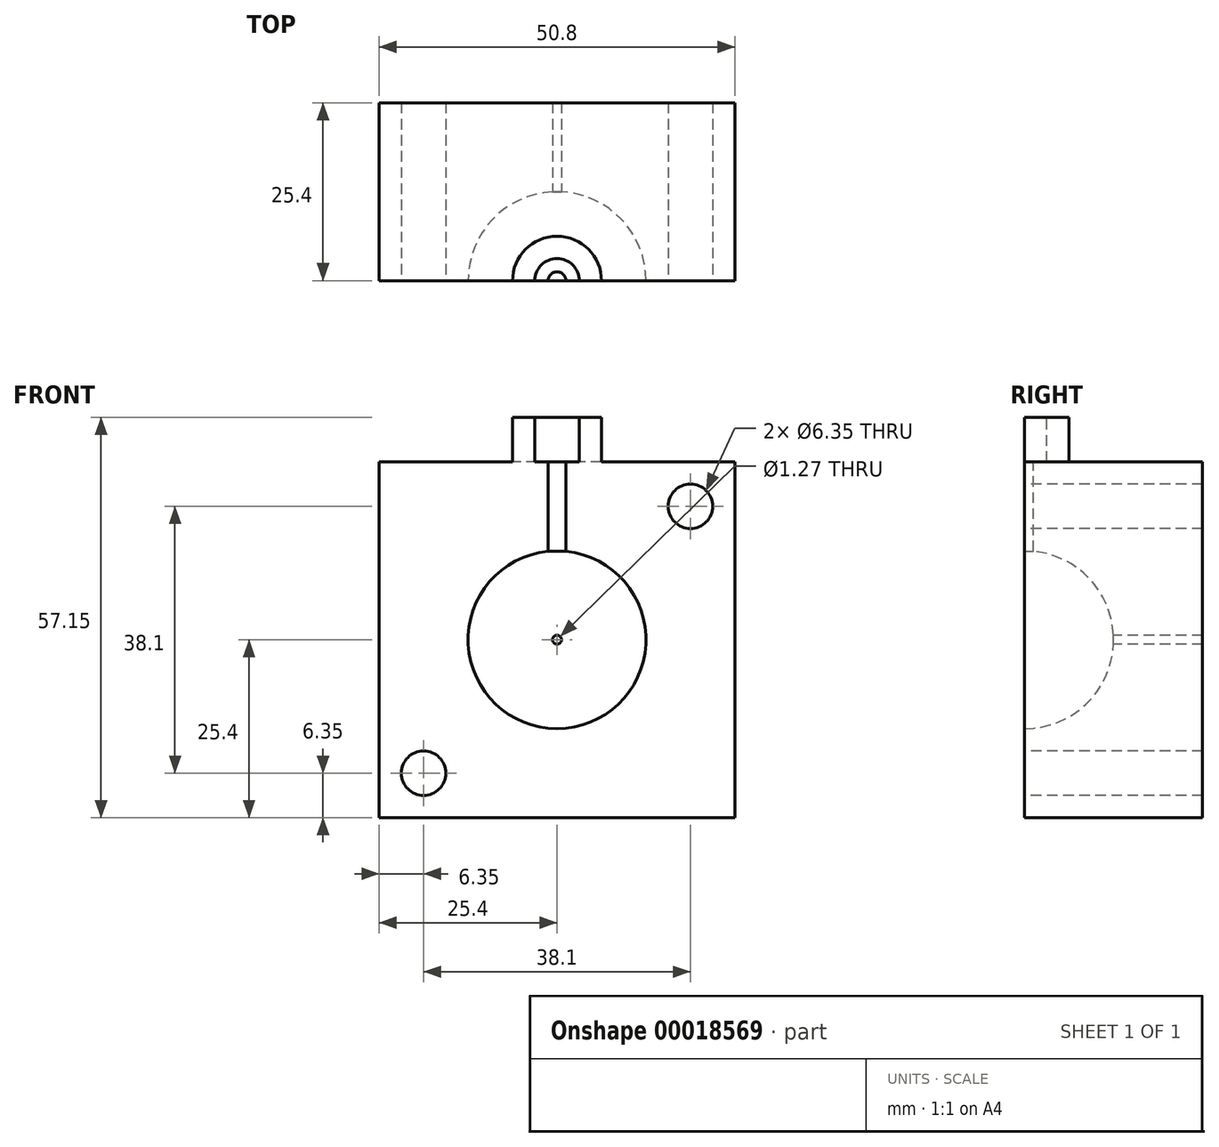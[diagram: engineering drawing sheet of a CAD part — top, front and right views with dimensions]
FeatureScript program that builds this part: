
annotation { "Feature Type Name" : "Feature", "Feature Type Description" : "" }
export const myFeature = defineFeature(function(context is Context, id is Id, definition is map)
    precondition{}
    {
        {
            var Q0;
            Q0=qCreatedBy(makeId("Front.planeOp"),FACE);
            var sketch = newSketch(context, id + "F0", { "sketchPlane" : qUnion([Q0])});
            skLineSegment(sketch, "E0.bottom", {"start": v(0, 0) * mm, "end": v(50.8, 0) * mm});
            skLineSegment(sketch, "E0.top", {"start": v(0, 50.8) * mm, "end": v(50.8, 50.8) * mm});
            skLineSegment(sketch, "E0.left", {"start": v(0, 0) * mm, "end": v(0, 50.8) * mm});
            skLineSegment(sketch, "E0.right", {"start": v(50.8, 0) * mm, "end": v(50.8, 50.8) * mm});
            skSolve(sketch);
        }
        {
            var Q0;
            Q0 = qSketchRegion(id + "F0", true);
            extrude(context, id + "F9", {"entities" : qUnion([Q0]), "depth" : 25.4 * mm});
        }
        {
            var Q0;
            Q0=makeQuery(id+"F9.opExtrude","CAP_FACE",FACE,{"disambiguationData":[OSD([sQuery(id+"F0.wireOp",EDGE,"E0.bottom"),sQuery(id+"F0.wireOp",EDGE,"E0.top"),sQuery(id+"F0.wireOp",EDGE,"E0.left"),sQuery(id+"F0.wireOp",EDGE,"E0.right")])],"isStart":false});
            var sketch = newSketch(context, id + "F1", { "sketchPlane" : qUnion([Q0])});
            skLineSegment(sketch, "E1", {"start": v(25.4, 50.8) * mm, "end": v(25.4, 0) * mm});
            skArc(sketch, "E2", {"start": v(25.4, 12.7) * mm, "mid": v(38.1, 25.4) * mm, "end": v(25.4, 38.1) * mm});
            skSolve(sketch);
        }
        {
            var Q0;
            Q0 = qSketchRegion(id + "F1", true);
            var Q1;
            Q1=sQuery(id+"F1.wireOp",EDGE,"E1");
            revolve(context, id + "F10", {"operationType" : NewBodyOperationType.REMOVE, "entities" : qUnion([Q0]), "axis" : qUnion([Q1]), "revolveType" : RevolveType.FULL, "oppositeDirection" : true});
        }
        {
            var Q0;
            Q0=makeQuery(id+"F9.opExtrude","CAP_FACE",FACE,{"disambiguationData":[OSD([sQuery(id+"F0.wireOp",EDGE,"E0.bottom"),sQuery(id+"F0.wireOp",EDGE,"E0.top"),sQuery(id+"F0.wireOp",EDGE,"E0.left"),sQuery(id+"F0.wireOp",EDGE,"E0.right")])],"isStart":false});
            var sketch = newSketch(context, id + "F11", { "sketchPlane" : qUnion([Q0])});
            skLineSegment(sketch, "E3", {"start": v(0, 0) * mm, "end": v(0, 6.35) * mm});
            skLineSegment(sketch, "E4", {"start": v(0, 0) * mm, "end": v(6.35, 0) * mm});
            skCircle(sketch, "E5", {"center": v(6.35, 6.35) * mm, "radius": 3.18 * mm});
            skSolve(sketch);
        }
        {
            var Q0;
            Q0 = qSketchRegion(id + "F11", true);
            extrude(context, id + "F2", {"entities" : qUnion([Q0]), "operationType" : NewBodyOperationType.REMOVE, "endBound" : BoundingType.THROUGH_ALL, "oppositeDirection" : true, "depth" : 25.4 * mm});
        }
        {
            var Q0;
            Q0=makeQuery(id+"F9.opExtrude","CAP_FACE",FACE,{"disambiguationData":[OSD([sQuery(id+"F0.wireOp",EDGE,"E0.bottom"),sQuery(id+"F0.wireOp",EDGE,"E0.top"),sQuery(id+"F0.wireOp",EDGE,"E0.left"),sQuery(id+"F0.wireOp",EDGE,"E0.right")])],"isStart":false});
            var sketch = newSketch(context, id + "F3", { "sketchPlane" : qUnion([Q0])});
            skLineSegment(sketch, "E6", {"start": v(50.8, 50.8) * mm, "end": v(44.45, 50.8) * mm});
            skLineSegment(sketch, "E7", {"start": v(50.8, 50.8) * mm, "end": v(50.8, 44.45) * mm});
            skCircle(sketch, "E8", {"center": v(44.45, 44.45) * mm, "radius": 3.18 * mm});
            skSolve(sketch);
        }
        {
            var Q0;
            Q0 = qSketchRegion(id + "F3", true);
            extrude(context, id + "F4", {"entities" : qUnion([Q0]), "operationType" : NewBodyOperationType.REMOVE, "endBound" : BoundingType.THROUGH_ALL, "oppositeDirection" : true, "depth" : 25.4 * mm});
        }
        {
            var Q0;
            Q0=makeQuery(id+"F9.opExtrude","SWEPT_FACE",FACE,{"disambiguationData":[OSD([sQuery(id+"F0.wireOp",EDGE,"E0.top")])]});
            var sketch = newSketch(context, id + "F5", { "sketchPlane" : qUnion([Q0])});
            skPoint(sketch, "E9.start.orphan", {"position": v(25.4, -25.4) * mm});
            skLineSegment(sketch, "E10", {"start": v(19.05, -25.4) * mm, "end": v(31.75, -25.4) * mm});
            skArc(sketch, "E11", {"start": v(31.75, -25.4) * mm, "mid": v(25.4, -19.05) * mm, "end": v(19.05, -25.4) * mm});
            skSolve(sketch);
        }
        {
            var Q0;
            Q0 = qSketchRegion(id + "F5", true);
            extrude(context, id + "F6", {"entities" : qUnion([Q0]), "operationType" : NewBodyOperationType.ADD, "depth" : 6.35 * mm});
        }
        {
            var Q0;
            Q0=makeQuery(id+"F6.opExtrude","CAP_FACE",FACE,{"disambiguationData":[OSD([sQuery(id+"F5.wireOp",EDGE,"E10"),sQuery(id+"F5.wireOp",EDGE,"E11")])],"isStart":false});
            var sketch = newSketch(context, id + "F7", { "sketchPlane" : qUnion([Q0])});
            skLineSegment(sketch, "E12", {"start": v(22.23, -25.4) * mm, "end": v(28.58, -25.4) * mm});
            skArc(sketch, "E13", {"start": v(28.58, -25.4) * mm, "mid": v(25.4, -22.23) * mm, "end": v(22.23, -25.4) * mm});
            skPoint(sketch, "E14.orphan", {"position": v(19.05, -25.4) * mm});
            skPoint(sketch, "E15.orphan", {"position": v(31.75, -25.4) * mm});
            skSolve(sketch);
        }
        {
            var Q0;
            Q0 = qSketchRegion(id + "F7", true);
            extrude(context, id + "F12", {"entities" : qUnion([Q0]), "operationType" : NewBodyOperationType.REMOVE, "oppositeDirection" : true, "depth" : 6.35 * mm});
        }
        {
            var Q0;
            Q0=makeQuery(id+"F12.boolean.opBoolean","COPY",FACE,{"derivedFrom":makeQuery(id+"F12.opExtrude","CAP_FACE",FACE,{"disambiguationData":[OSD([sQuery(id+"F7.wireOp",EDGE,"E12"),sQuery(id+"F7.wireOp",EDGE,"E13")])],"isStart":false})});
            var sketch = newSketch(context, id + "F13", { "sketchPlane" : qUnion([Q0])});
            skLineSegment(sketch, "E16", {"start": v(22.23, -25.4) * mm, "end": v(28.58, -25.4) * mm});
            skCircle(sketch, "E17", {"center": v(25.4, -25.4) * mm, "radius": 1.27 * mm});
            skSolve(sketch);
        }
        {
            var Q0;
            Q0 = qSketchRegion(id + "F13", true);
            extrude(context, id + "F8", {"entities" : qUnion([Q0]), "operationType" : NewBodyOperationType.REMOVE, "oppositeDirection" : true, "depth" : 25.4 * mm});
        }
        {
            var Q0;
            Q0=makeQuery(id+"F6.boolean.opBoolean","MERGE",FACE,{"derivedFrom":[makeQuery(id+"F9.opExtrude","CAP_FACE",FACE,{"disambiguationData":[OSD([sQuery(id+"F0.wireOp",EDGE,"E0.bottom"),sQuery(id+"F0.wireOp",EDGE,"E0.top"),sQuery(id+"F0.wireOp",EDGE,"E0.left"),sQuery(id+"F0.wireOp",EDGE,"E0.right")])],"isStart":false}),makeQuery(id+"F6.opExtrude","SWEPT_FACE",FACE,{"disambiguationData":[OSD([sQuery(id+"F5.wireOp",EDGE,"E10")])]})]});
            var sketch = newSketch(context, id + "F14", { "sketchPlane" : qUnion([Q0])});
            skLineSegment(sketch, "E18", {"start": v(24.77, 25.4) * mm, "end": v(25.4, 25.4) * mm});
            skCircle(sketch, "E19", {"center": v(25.4, 25.4) * mm, "radius": 0.64 * mm});
            skPoint(sketch, "E20.orphan", {"position": v(50.8, 25.4) * mm});
            skPoint(sketch, "E21.orphan", {"position": v(0, 25.4) * mm});
            skSolve(sketch);
        }
        {
            var Q0;
            Q0 = qSketchRegion(id + "F14", true);
            extrude(context, id + "F15", {"entities" : qUnion([Q0]), "operationType" : NewBodyOperationType.REMOVE, "endBound" : BoundingType.THROUGH_ALL, "oppositeDirection" : true, "depth" : 25.4 * mm});
        }
    });
